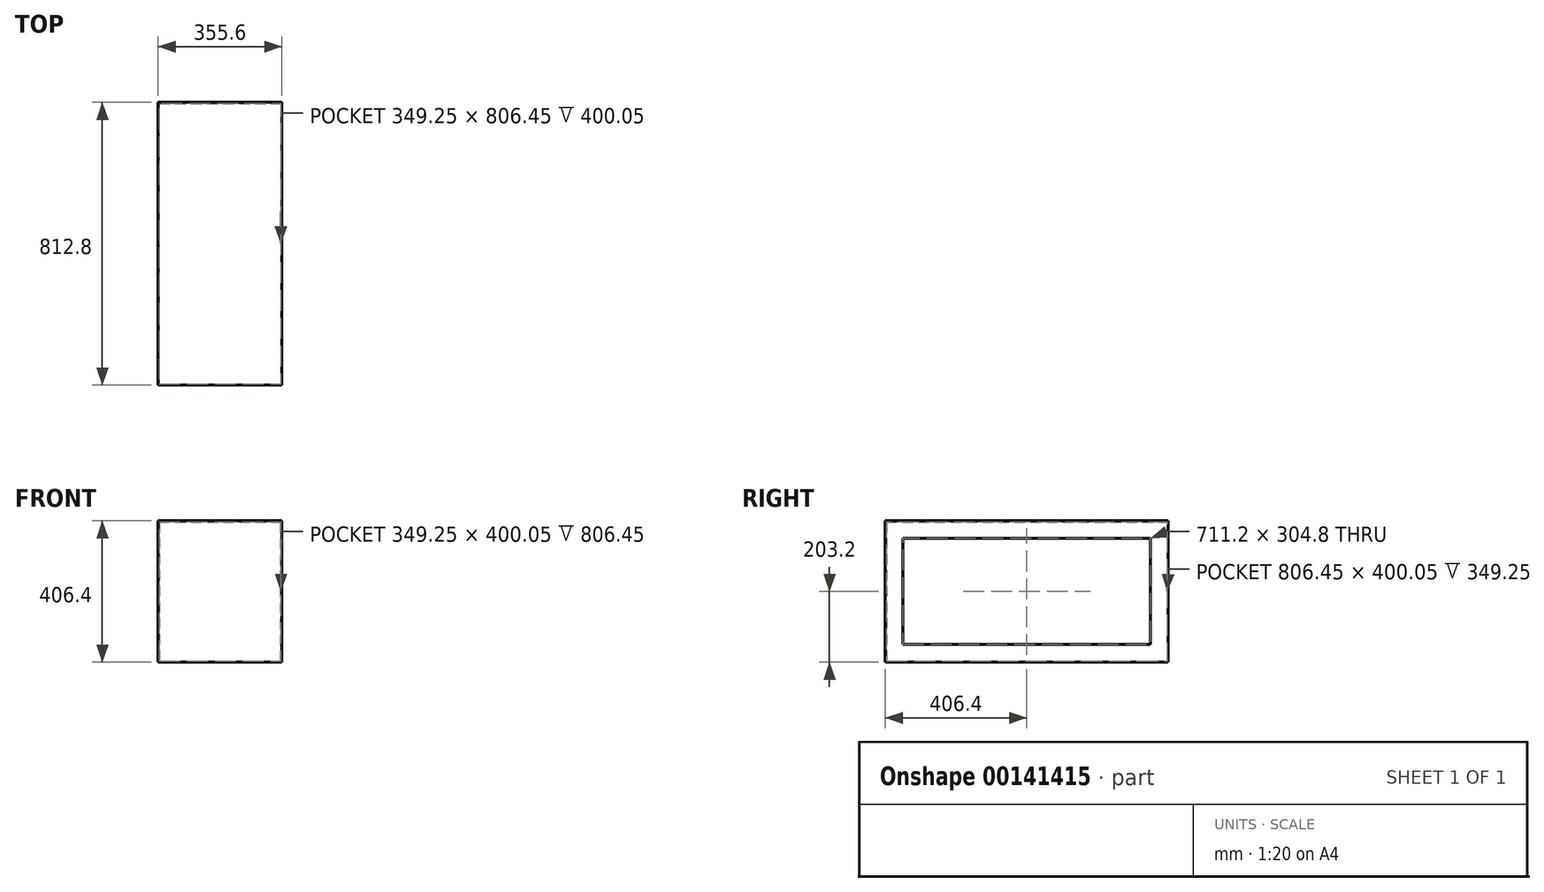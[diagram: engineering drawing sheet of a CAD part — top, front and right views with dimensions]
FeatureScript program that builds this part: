
annotation { "Feature Type Name" : "Feature", "Feature Type Description" : "" }
export const myFeature = defineFeature(function(context is Context, id is Id, definition is map)
    precondition{}
    {
        {
            var Q0;
            Q0=qCreatedBy(makeId("Right.planeOp"),FACE);
            var sketch = newSketch(context, id + "F0", { "sketchPlane" : qUnion([Q0])});
            skLineSegment(sketch, "E0.bottom", {"start": v(-406.4, 203.2) * mm, "end": v(406.4, 203.2) * mm});
            skLineSegment(sketch, "E0.top", {"start": v(-406.4, -203.2) * mm, "end": v(406.4, -203.2) * mm});
            skLineSegment(sketch, "E0.left", {"start": v(-406.4, 203.2) * mm, "end": v(-406.4, -203.2) * mm});
            skLineSegment(sketch, "E0.right", {"start": v(406.4, 203.2) * mm, "end": v(406.4, -203.2) * mm});
            skPoint(sketch, "E0.middle", {"position": v(0, 0) * mm});
            skSolve(sketch);
        }
        {
            var Q0;
            Q0 = qSketchRegion(id + "F0", true);
            extrude(context, id + "F1", {"entities" : qUnion([Q0]), "oppositeDirection" : true, "depth" : 355.6 * mm});
        }
        {
            var Q0;
            Q0=makeQuery(id+"F1.opExtrude","CAP_FACE",FACE,{"disambiguationData":[OSD([sQuery(id+"F0.wireOp",EDGE,"E0.bottom"),sQuery(id+"F0.wireOp",EDGE,"E0.top"),sQuery(id+"F0.wireOp",EDGE,"E0.left"),sQuery(id+"F0.wireOp",EDGE,"E0.right")])],"isStart":true});
            var sketch = newSketch(context, id + "F2", { "sketchPlane" : qUnion([Q0])});
            skLineSegment(sketch, "E1.bottom", {"start": v(-355.6, 152.4) * mm, "end": v(355.6, 152.4) * mm});
            skLineSegment(sketch, "E1.top", {"start": v(-355.6, -152.4) * mm, "end": v(355.6, -152.4) * mm});
            skLineSegment(sketch, "E1.left", {"start": v(-355.6, 152.4) * mm, "end": v(-355.6, -152.4) * mm});
            skLineSegment(sketch, "E1.right", {"start": v(355.6, 152.4) * mm, "end": v(355.6, -152.4) * mm});
            skPoint(sketch, "E1.middle", {"position": v(0, 0) * mm});
            skSolve(sketch);
        }
        {
            var Q0;
            Q0 = qSketchRegion(id + "F2", true);
            extrude(context, id + "F3", {"entities" : qUnion([Q0]), "operationType" : NewBodyOperationType.REMOVE, "oppositeDirection" : true, "depth" : 352.42 * mm});
        }
        {
            var Q0;
            Q0=makeQuery(id+"F3.boolean.opBoolean","COPY",FACE,{"derivedFrom":makeQuery(id+"F3.opExtrude","SWEPT_FACE",FACE,{"disambiguationData":[OSD([sQuery(id+"F2.wireOp",EDGE,"E1.left")])]})});
            var sketch = newSketch(context, id + "F4", { "sketchPlane" : qUnion([Q0])});
            skLineSegment(sketch, "E2.bottom", {"start": v(3.17, 152.4) * mm, "end": v(352.43, 152.4) * mm});
            skLineSegment(sketch, "E2.top", {"start": v(3.18, -152.4) * mm, "end": v(352.43, -152.4) * mm});
            skLineSegment(sketch, "E2.left", {"start": v(3.17, 152.4) * mm, "end": v(3.18, -152.4) * mm});
            skLineSegment(sketch, "E2.right", {"start": v(352.43, 152.4) * mm, "end": v(352.43, -152.4) * mm});
            skSolve(sketch);
        }
        {
            var Q0;
            Q0 = qSketchRegion(id + "F4", true);
            extrude(context, id + "F5", {"entities" : qUnion([Q0]), "operationType" : NewBodyOperationType.REMOVE, "oppositeDirection" : true, "depth" : 47.62 * mm});
        }
        {
            var Q0;
            Q0=makeQuery(id+"F3.boolean.opBoolean","COPY",FACE,{"derivedFrom":makeQuery(id+"F3.opExtrude","SWEPT_FACE",FACE,{"disambiguationData":[OSD([sQuery(id+"F2.wireOp",EDGE,"E1.right")])]})});
            var sketch = newSketch(context, id + "F6", { "sketchPlane" : qUnion([Q0])});
            skLineSegment(sketch, "E3.bottom", {"start": v(-352.43, -152.4) * mm, "end": v(-3.17, -152.4) * mm});
            skLineSegment(sketch, "E3.top", {"start": v(-352.43, 152.4) * mm, "end": v(-3.18, 152.4) * mm});
            skLineSegment(sketch, "E3.left", {"start": v(-352.43, -152.4) * mm, "end": v(-352.43, 152.4) * mm});
            skLineSegment(sketch, "E3.right", {"start": v(-3.17, -152.4) * mm, "end": v(-3.18, 152.4) * mm});
            skSolve(sketch);
        }
        {
            var Q0;
            Q0 = qSketchRegion(id + "F6", true);
            extrude(context, id + "F7", {"entities" : qUnion([Q0]), "operationType" : NewBodyOperationType.REMOVE, "oppositeDirection" : true, "depth" : 47.62 * mm});
        }
        {
            var Q0;
            Q0=makeQuery(id+"F7.boolean.opBoolean","MERGE",FACE,{"derivedFrom":[makeQuery(id+"F5.boolean.opBoolean","MERGE",FACE,{"derivedFrom":[makeQuery(id+"F3.boolean.opBoolean","COPY",FACE,{"derivedFrom":makeQuery(id+"F3.opExtrude","SWEPT_FACE",FACE,{"disambiguationData":[OSD([sQuery(id+"F2.wireOp",EDGE,"E1.top")])]})}),makeQuery(id+"F5.opExtrude","SWEPT_FACE",FACE,{"disambiguationData":[OSD([sQuery(id+"F4.wireOp",EDGE,"E2.top")])]})]}),makeQuery(id+"F7.opExtrude","SWEPT_FACE",FACE,{"disambiguationData":[OSD([sQuery(id+"F6.wireOp",EDGE,"E3.bottom")])]})]});
            var sketch = newSketch(context, id + "F8", { "sketchPlane" : qUnion([Q0])});
            skLineSegment(sketch, "E4.bottom", {"start": v(-352.43, 403.23) * mm, "end": v(-3.18, 403.23) * mm});
            skLineSegment(sketch, "E4.top", {"start": v(-352.43, -403.23) * mm, "end": v(-3.18, -403.23) * mm});
            skLineSegment(sketch, "E4.left", {"start": v(-352.43, 403.23) * mm, "end": v(-352.43, -403.23) * mm});
            skLineSegment(sketch, "E4.right", {"start": v(-3.18, 403.23) * mm, "end": v(-3.18, -403.23) * mm});
            skSolve(sketch);
        }
        {
            var Q0;
            Q0 = qSketchRegion(id + "F8", true);
            extrude(context, id + "F9", {"entities" : qUnion([Q0]), "operationType" : NewBodyOperationType.REMOVE, "oppositeDirection" : true, "depth" : 47.62 * mm});
        }
        {
            var Q0;
            Q0=makeQuery(id+"F7.boolean.opBoolean","MERGE",FACE,{"derivedFrom":[makeQuery(id+"F5.boolean.opBoolean","MERGE",FACE,{"derivedFrom":[makeQuery(id+"F3.boolean.opBoolean","COPY",FACE,{"derivedFrom":makeQuery(id+"F3.opExtrude","SWEPT_FACE",FACE,{"disambiguationData":[OSD([sQuery(id+"F2.wireOp",EDGE,"E1.bottom")])]})}),makeQuery(id+"F5.opExtrude","SWEPT_FACE",FACE,{"disambiguationData":[OSD([sQuery(id+"F4.wireOp",EDGE,"E2.bottom")])]})]}),makeQuery(id+"F7.opExtrude","SWEPT_FACE",FACE,{"disambiguationData":[OSD([sQuery(id+"F6.wireOp",EDGE,"E3.top")])]})]});
            var sketch = newSketch(context, id + "F10", { "sketchPlane" : qUnion([Q0])});
            skLineSegment(sketch, "E5.bottom", {"start": v(-352.43, -403.23) * mm, "end": v(-3.18, -403.23) * mm});
            skLineSegment(sketch, "E5.top", {"start": v(-352.43, 403.23) * mm, "end": v(-3.18, 403.23) * mm});
            skLineSegment(sketch, "E5.left", {"start": v(-352.43, -403.23) * mm, "end": v(-352.43, 403.23) * mm});
            skLineSegment(sketch, "E5.right", {"start": v(-3.18, -403.23) * mm, "end": v(-3.18, 403.23) * mm});
            skSolve(sketch);
        }
        {
            var Q0;
            Q0 = qSketchRegion(id + "F10", true);
            extrude(context, id + "F11", {"entities" : qUnion([Q0]), "operationType" : NewBodyOperationType.REMOVE, "oppositeDirection" : true, "depth" : 47.62 * mm});
        }
    });
